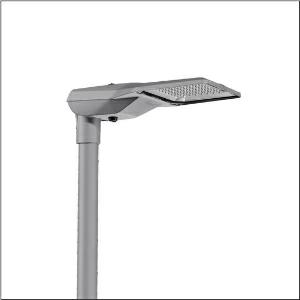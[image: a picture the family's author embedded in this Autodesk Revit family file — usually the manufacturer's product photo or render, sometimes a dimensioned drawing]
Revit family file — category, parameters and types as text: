
# Revit family: streetlight_sl_21_iq_midi___st0_8a_5xe3c31y08mb_7afc
name_source: partatom
category: Lighting Fixtures
units: mm (PartAtom-declared; Revit-internal decimal feet)

## family parameters
Cut with Voids When Loaded = No
Host = Face
Light Source = No
Part Type = Normal
Room Calculation Point = No
Round Connector Dimension = Use Diameter
Shared = No

## types (1)
- --- (1 x LED, 18340 lm, 129.3 W, 3000K)
    Apparent Load = 129 VA
    CIE Flux Codes = 38 75 97 100 100
    Color Rendering = 70
    Color Temperature = 3000K
    Default Elevation = 1800 mm
    Description = Streetlight SL 21 iQ midi, mast luminaire, primary light control with lens, of PMMA, primary optical cover: cover, of toughened safety glass, transparent, light distribution: ST0.8a, light emission: direct distribution, primary light characteristic: asymmetric, installation type: post-top, side-entry, LED, High Power LED, rated luminous flux: 18.340lm, luminous efficacy: 142lm/W, light colour: 730, colour temperature: 3000K, control: presetting dimming logarithmic, Street-Remote, Auto-Match, Temp-Guard, Lumen-Switch, Night-Set, Smart-Wire, Light-Fading, Desk-Remote (wireless, voltage-free reading and setting of iQ features in the workshop via application-optimized NFC function/RFID function), optimised constant luminous flux control (CLO 2.0), mains connection: 230..240V, AC, 50/60Hz, start of lifetime: 129W, end of service life: 142W, reduction: 56W, luminaire housing, of diecast aluminium, powder-coated, Siteco® metallic grey (DB 702S), corrosivity category C5 mid according to DIN EN ISO 12944, please order mast flange separately, inclination adjustable: 0°, 5°, 10°, 15°, sealing non-destructively replaceable, multi-level sealing system, length: 644mm, width: 335mm, height: 110mm, mast flange for spigot size: 42mm (side-entry): 5XC10008XM4, 60/48mm (side-entry/post-top): 5XC10108XM2, 76/60mm (side-entry/post-top): 5XC10108XM1, Smart Interface below and above, protection rating (complete): IP66, insulation class (complete): insulation class II (safety insulation), certification: CE, ENEC, ENEC+, VDE, impact resistance: IK09, permissible operating ambient temperature for outdoor applications: -40..+50°C, standard-compliant lighting for roads and squares, packaging unit: 1 piece

Light Distribution: ST0.8a
    Height = 111 mm
    Lamp = 1 x LED
    Lamp Light Flux = 18340 lm
    Lamp Power = 129.3 W
    Lamp count = 1
    Length = 644 mm
    Luminous efficacy = 142 lm/W
    Manufacturer = Siteco
    ModVariant = No
    Model = 5XE3C31Y08MB
    Number of Poles = 1
    OnlyDefault = Yes
    Power Factor = 1
    Product Name = Streetlight SL 21 iQ midi | ST0.8a
    Product group = mast luminaire | pylon top
    ProductGroupID = 6100
    Protection Class = Protection class II
    Protection Degree = IP 66
    RLX_Detail_Level = 1
    RLX_Emergency_Light_Flux = 0 lm
    RLX_Emergency_Type = 0
    RLX_Emergency_Type_DB = No
    RlxData = <blob elided: 91301 chars, md5=c964f5dd>
    Socket = socket
    Standby Power = 0 W
    System Light Flux = 18340 lm
    System Power = 129 W
    Type Comments = factory setting: luminous flux: 100 % | dim-lin: 254 | 672 mA
    Type Image = l_1004304.jpg
    URL = http://relux.com
    VarID = @adj_061467
    Voltage = 0 V
    Weight = 0.00 kg
    Width = 336 mm

## geometry (parser evidence)
native form markers: Blend x4, Sweep x10
no freeform markers — native parametric forms only
